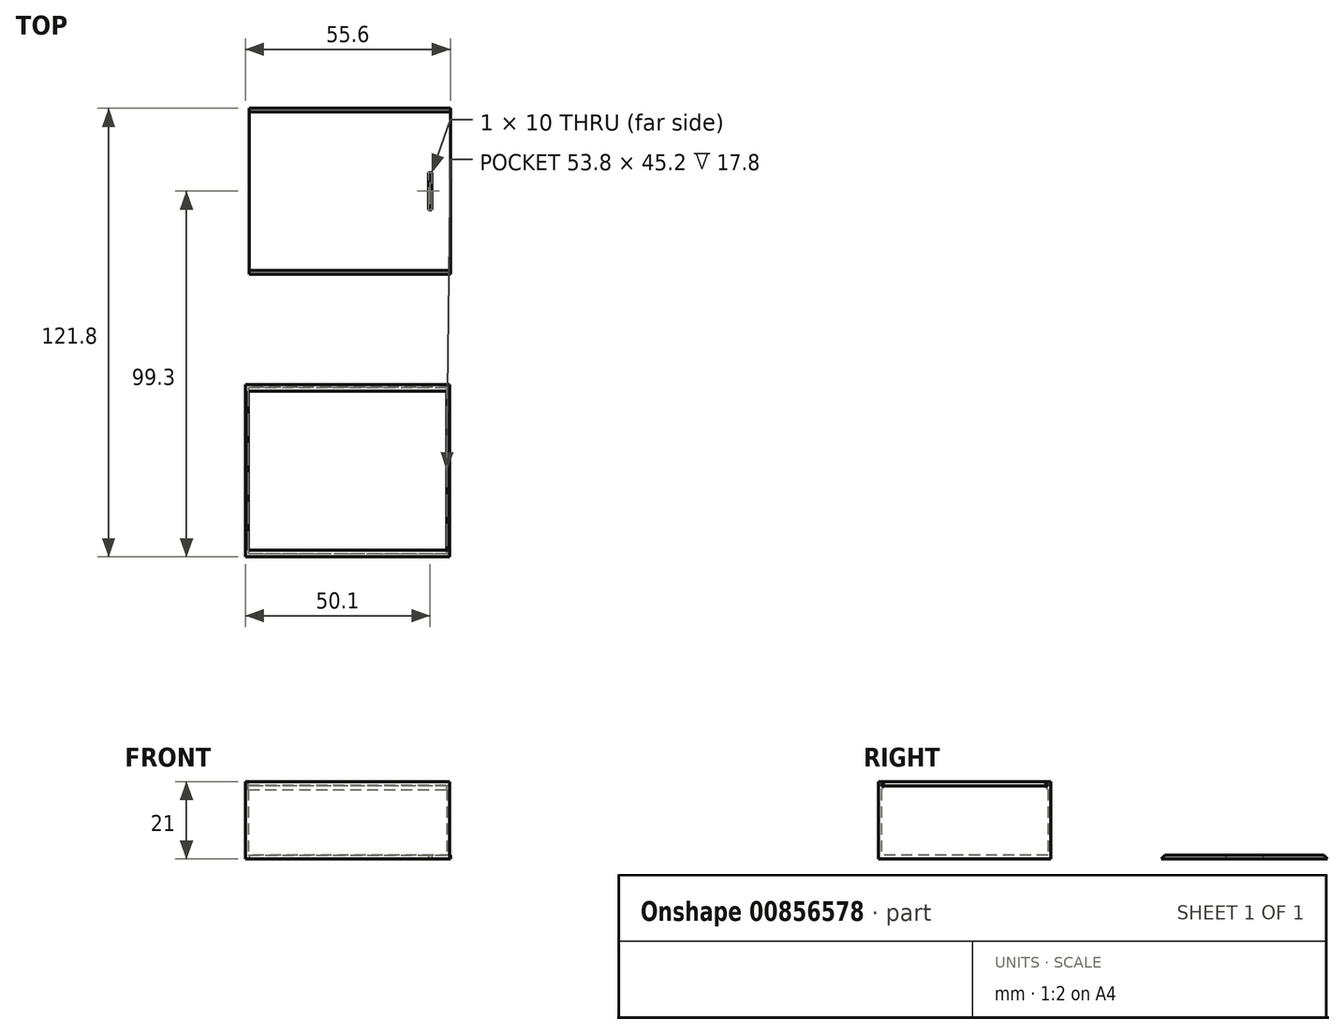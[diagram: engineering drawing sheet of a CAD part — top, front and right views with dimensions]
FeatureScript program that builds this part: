
annotation { "Feature Type Name" : "Feature", "Feature Type Description" : "" }
export const myFeature = defineFeature(function(context is Context, id is Id, definition is map)
    precondition{}
    {
        {
            var Q0;
            Q0=qCreatedBy(makeId("Top.planeOp"),FACE);
            var sketch = newSketch(context, id + "F0", { "sketchPlane" : qUnion([Q0])});
            skLineSegment(sketch, "E0.bottom", {"start": v(0, 0) * mm, "end": v(53.8, 0) * mm});
            skLineSegment(sketch, "E0.top", {"start": v(0, -45.2) * mm, "end": v(53.8, -45.2) * mm});
            skLineSegment(sketch, "E0.left", {"start": v(0, 0) * mm, "end": v(0, -45.2) * mm});
            skLineSegment(sketch, "E0.right", {"start": v(53.8, 0) * mm, "end": v(53.8, -45.2) * mm});
            skLineSegment(sketch, "E1.0", {"start": v(-0.8, 0.8) * mm, "end": v(54.6, 0.8) * mm});
            skLineSegment(sketch, "E1.1", {"start": v(-0.8, 0.8) * mm, "end": v(-0.8, -46) * mm});
            skLineSegment(sketch, "E1.2", {"start": v(-0.8, -46) * mm, "end": v(54.6, -46) * mm});
            skLineSegment(sketch, "E1.3", {"start": v(54.6, 0.8) * mm, "end": v(54.6, -46) * mm});
            skLineSegment(sketch, "E2.bottom", {"start": v(54.8, 30.8) * mm, "end": v(0.2, 30.8) * mm});
            skLineSegment(sketch, "E2.top", {"start": v(54.8, 75.8) * mm, "end": v(0.2, 75.8) * mm});
            skLineSegment(sketch, "E2.left", {"start": v(54.8, 30.8) * mm, "end": v(54.8, 75.8) * mm});
            skLineSegment(sketch, "E2.right", {"start": v(0.2, 30.8) * mm, "end": v(0.2, 75.8) * mm});
            skLineSegment(sketch, "E3.bottom", {"start": v(48.8, 48.3) * mm, "end": v(49.8, 48.3) * mm});
            skLineSegment(sketch, "E3.top", {"start": v(48.8, 58.3) * mm, "end": v(49.8, 58.3) * mm});
            skLineSegment(sketch, "E3.left", {"start": v(48.8, 48.3) * mm, "end": v(48.8, 58.3) * mm});
            skLineSegment(sketch, "E3.right", {"start": v(49.8, 48.3) * mm, "end": v(49.8, 58.3) * mm});
            skLineSegment(sketch, "E4", {"start": v(54.8, 53.3) * mm, "end": v(0.2, 53.3) * mm, "construction": true});
            skLineSegment(sketch, "E5", {"start": v(49.8, 53.3) * mm, "end": v(48.8, 53.3) * mm, "construction": true});
            skSolve(sketch);
        }
        {
            var Q0;
            Q0=makeQuery(id+"F0.imprint","IMPRINT",FACE,{"disambiguationData":[TD([[makeQuery(id+"F0.imprint","IMPRINT",EDGE,{"derivedFrom":sQuery(id+"F0.wireOp",EDGE,"E0.bottom")}),1.0]])]});
            extrude(context, id + "F1", {"entities" : qUnion([Q0]), "depth" : 21 * mm, "offsetDistance" : 25 * mm});
        }
        {
            var Q0;
            Q0=makeQuery(id+"F0.imprint","IMPRINT",FACE,{"disambiguationData":[TD([[makeQuery(id+"F0.imprint","IMPRINT",EDGE,{"derivedFrom":sQuery(id+"F0.wireOp",EDGE,"E0.bottom")}),-1.0]])]});
            var Q1;
            Q1=makeQuery(id+"F0.imprint","IMPRINT",FACE,{"disambiguationData":[TD([[makeQuery(id+"F0.imprint","IMPRINT",EDGE,{"derivedFrom":sQuery(id+"F0.wireOp",EDGE,"dxKq3VSe-QV8x-4qvb-WFEf-KZVt2BvtcllD")}),-1.0]])]});
            var Q2;
            Q2=makeQuery(id+"F0.imprint","IMPRINT",FACE,{"disambiguationData":[TD([[makeQuery(id+"F0.imprint","IMPRINT",EDGE,{"derivedFrom":sQuery(id+"F0.wireOp",EDGE,"dxKq3VSe-QV8x-4qvb-WFEf-KZVt2BvtcllD")}),1.0]])]});
            var Q3;
            Q3=makeQuery(id+"F0.imprint","IMPRINT",FACE,{"disambiguationData":[TD([[makeQuery(id+"F0.imprint","IMPRINT",EDGE,{"derivedFrom":sQuery(id+"F0.wireOp",EDGE,"34a8a779-3f46-43d9-b586-0b6456db9051")}),-1.0]])]});
            var Q4;
            Q4=makeQuery(id+"F0.imprint","IMPRINT",FACE,{"disambiguationData":[TD([[makeQuery(id+"F0.imprint","IMPRINT",EDGE,{"derivedFrom":sQuery(id+"F0.wireOp",EDGE,"34a8a779-3f46-43d9-b586-0b6456db9051")}),1.0]])]});
            extrude(context, id + "F2", {"entities" : qUnion([Q0, Q1, Q2, Q3, Q4]), "operationType" : NewBodyOperationType.ADD, "depth" : 1 * mm, "offsetDistance" : 25 * mm});
        }
        {
            var Q0;
            Q0=makeQuery(id+"F1.opExtrude","SWEPT_FACE",FACE,{"disambiguationData":[OSD([sQuery(id+"F0.wireOp",EDGE,"E0.top")])]});
            var sketch = newSketch(context, id + "F3", { "sketchPlane" : qUnion([Q0])});
            skLineSegment(sketch, "E6", {"start": v(-53.8, 20) * mm, "end": v(0, 20) * mm});
            skLineSegment(sketch, "E7", {"start": v(-53.8, 19.8) * mm, "end": v(0, 19.8) * mm});
            skLineSegment(sketch, "E8", {"start": v(-53.8, 18.8) * mm, "end": v(0, 18.8) * mm});
            skSolve(sketch);
        }
        {
            var Q0;
            Q0=makeQuery(id+"F1.opExtrude","SWEPT_FACE",FACE,{"disambiguationData":[OSD([sQuery(id+"F0.wireOp",EDGE,"E0.bottom")])]});
            var sketch = newSketch(context, id + "F4", { "sketchPlane" : qUnion([Q0])});
            skLineSegment(sketch, "E9", {"start": v(0, 20) * mm, "end": v(53.8, 20) * mm});
            skLineSegment(sketch, "E10", {"start": v(53.8, 19.8) * mm, "end": v(0, 19.8) * mm});
            skLineSegment(sketch, "E11", {"start": v(0, 18.8) * mm, "end": v(53.8, 18.8) * mm});
            skSolve(sketch);
        }
        {
            var Q0;
            {var subQ0=sQuery(id+"F3.wireOp",EDGE,"E6");Q0=makeQuery(id+"F3.imprint","IMPRINT",FACE,{"disambiguationData":[TD([[makeQuery(id+"F3.imprint","IMPRINT",EDGE,{"derivedFrom":subQ0}),1.0]])]});}
            var Q1;
            {var subQ0=sQuery(id+"F3.wireOp",EDGE,"E7");Q1=makeQuery(id+"F3.imprint","IMPRINT",FACE,{"disambiguationData":[TD([[makeQuery(id+"F3.imprint","IMPRINT",EDGE,{"derivedFrom":subQ0}),-1.0]])]});}
            extrude(context, id + "F5", {"entities" : qUnion([Q0, Q1]), "operationType" : NewBodyOperationType.ADD, "depth" : 1 * mm, "offsetDistance" : 25 * mm});
        }
        {
            var Q0;
            {var subQ0=sQuery(id+"F4.wireOp",EDGE,"E10");Q0=makeQuery(id+"F4.imprint","IMPRINT",FACE,{"disambiguationData":[TD([[makeQuery(id+"F4.imprint","IMPRINT",EDGE,{"derivedFrom":subQ0}),1.0]])]});}
            var Q1;
            {var subQ0=sQuery(id+"F4.wireOp",EDGE,"E9");Q1=makeQuery(id+"F4.imprint","IMPRINT",FACE,{"disambiguationData":[TD([[makeQuery(id+"F4.imprint","IMPRINT",EDGE,{"derivedFrom":subQ0}),1.0]])]});}
            extrude(context, id + "F6", {"entities" : qUnion([Q0, Q1]), "operationType" : NewBodyOperationType.ADD, "depth" : 1 * mm, "offsetDistance" : 25 * mm});
        }
        {
            var Q0;
            Q0=makeQuery(id+"F6.opExtrude","CAP_EDGE",EDGE,{"disambiguationData":[OSD([sQuery(id+"F4.wireOp",EDGE,"E11")])],"isStart":false});
            var Q1;
            Q1=makeQuery(id+"F6.opExtrude","CAP_EDGE",EDGE,{"disambiguationData":[OSD([sQuery(id+"F4.wireOp",EDGE,"E9")])],"isStart":false});
            var Q2;
            Q2=makeQuery(id+"F5.opExtrude","CAP_EDGE",EDGE,{"disambiguationData":[OSD([sQuery(id+"F3.wireOp",EDGE,"E8")])],"isStart":false});
            var Q3;
            Q3=makeQuery(id+"F5.opExtrude","CAP_EDGE",EDGE,{"disambiguationData":[OSD([sQuery(id+"F3.wireOp",EDGE,"E6")])],"isStart":false});
            chamfer(context, id + "F7", {"entities" : qUnion([Q0, Q1, Q2, Q3]), "width" : 1 * mm, "tangentPropagation" : true});
        }
        {
            var Q0;
            Q0=makeQuery(id+"F1.opExtrude","SWEPT_FACE",FACE,{"disambiguationData":[OSD([sQuery(id+"F0.wireOp",EDGE,"E0.right")])]});
            var sketch = newSketch(context, id + "F8", { "sketchPlane" : qUnion([Q0])});
            skLineSegment(sketch, "E12", {"start": v(1, 19.8) * mm, "end": v(44.2, 19.8) * mm});
            skSolve(sketch);
        }
        {
            var Q0;
            Q0=makeQuery(id+"F8.imprint","IMPRINT",FACE,{"disambiguationData":[TD([[makeQuery(id+"F8.imprint","IMPRINT",EDGE,{"derivedFrom":sQuery(id+"F8.wireOp",EDGE,"E12")}),1.0]])]});
            extrude(context, id + "F9", {"entities" : qUnion([Q0]), "operationType" : NewBodyOperationType.REMOVE, "endBound" : BoundingType.UP_TO_NEXT, "oppositeDirection" : true, "depth" : 25 * mm, "offsetDistance" : 25 * mm});
        }
        {
            var Q0;
            Q0=makeQuery(id+"F0.imprint","IMPRINT",FACE,{"disambiguationData":[TD([[makeQuery(id+"F0.imprint","IMPRINT",EDGE,{"derivedFrom":sQuery(id+"F0.wireOp",EDGE,"E2.bottom")}),-1.0]])]});
            extrude(context, id + "F10", {"entities" : qUnion([Q0]), "depth" : 1 * mm, "offsetDistance" : 25 * mm});
        }
        {
            var Q0;
            Q0=makeQuery(id+"F10.opExtrude","CAP_EDGE",EDGE,{"disambiguationData":[OSD([sQuery(id+"F0.wireOp",EDGE,"E2.bottom")])],"isStart":false});
            var Q1;
            Q1=makeQuery(id+"F10.opExtrude","CAP_EDGE",EDGE,{"disambiguationData":[OSD([sQuery(id+"F0.wireOp",EDGE,"E2.top")])],"isStart":false});
            chamfer(context, id + "F11", {"entities" : qUnion([Q0, Q1]), "width" : 1 * mm, "tangentPropagation" : true});
        }
    });
